# Revit family: ElectricalEquipment_Hager_TPNLighting&Power_250ATripleMeteredBoards
name_source: partatom
category: Electrical Equipment
revit_build: Autodesk Revit 2015 (Build: 20160512_1515(x64)
units: mm (PartAtom-declared; Revit-internal decimal feet)

## types (1)
- JKD2884PM
    Assembly Code = D5010
    AssetType = Fixed
    BIMObjectName = Hager_ElectricalEquipment_TripleMeteredBoards_JKD2884PM
    Category = ElectricalEquipment
    ClassificationName = Uniclass2015
    ClassificationValue = Pr_80_77_28_16
    Colour = RAL 9010 White Gloss
    Default Elevation = 500 mm
    Description = 200APower/Lighting/ServicesBoard.Lower8,Mid8,Top4Way.Pulsed/Modbus
    DocumentationLiterature = http://www.hager.co.uk
    DocumentationTechnical = http://www.hager.co.uk
    DurationUnit = Years
    EAN = 5015652600299
    ExpectedLife = 10
    Features = 200APower/Lighting/ServicesBoard.Lower8,Mid8,Top4Way.Pulsed/Modbus
    IfcExportAs = ElectricalEquipment
    Incoming = 125A
    Keynote = V
    Mains Type = AC
    Manufacturer = Hager
    ManufacturerName = Hager
    Material = MildSteel,ABS,AcousticComposite
    Model = JKD2884PM
    NBSDescription = ElectricalEquipment
    NBSObjectName = Hager_TripleMeteredBoards_JKD2884PM
    NBSReference = Pr_80_77_28_16
    Neutral Rating = 100.00%
    NominalDepth = 166 mm
    NominalHeight = 1850 mm  [stored 6.06955 ft]
    NominalLength = 0 mm  [stored 0 ft]
    NominalWidth = 465 mm
    Outgoing = 63A
    ReplacementCost = 0
    ServiceLifeDuration = 0
    Shape = Rectangular
    Type Comments = JKD2884PM
    TypeName = ElectricalEquipment
    URL = http://www.hager.co.uk
    Voltage = 230V
    WarrantyDescription = See Manufacturer
    WarrantyDurationLabor = 0
    WarrantyDurationParts = 2
    WarrantyDurationUnit = Years
    WarrantyGuarantorParts = 2
    _BimSpecGuid = 0
    _BimstoreBibleVersion = V14
    _CurrentRevision = 0
    _DistributedBy = www.bimstore.co.uk

note: [stored X ft] marks values corroborated as IEEE doubles in the binary element streams (Revit-internal decimal feet)

## geometry (parser evidence)
native form markers: Blend x4, Sweep x2
no freeform markers — native parametric forms only
